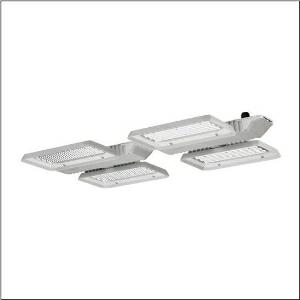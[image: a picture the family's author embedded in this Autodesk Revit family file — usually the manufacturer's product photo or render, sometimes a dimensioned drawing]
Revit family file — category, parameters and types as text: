
# Revit family: highbay_11_51hla1d24nca
name_source: partatom
category: Lighting Fixtures
units: mm (PartAtom-declared; Revit-internal decimal feet)

## family parameters
Cut with Voids When Loaded = No
Host = Face
Light Source = No
Part Type = Normal
Room Calculation Point = No
Round Connector Dimension = Use Diameter
Shared = No

## types (1)
- --- (1 x LED, 32370 lm, 189.6 W, 4000K)
    Apparent Load = 190 VA
    CIE Flux Codes = 88 95 99 100 99
    Color Rendering = 80
    Color Temperature = 4000K
    Default Elevation = 1800 mm
    Description = Highbay 11, LED high bay luminaire, primary light control with lens, of PMMA, light emission: direct distribution, primary light characteristic: symmetric, installation type: suspended mounting, surface-mounted, for 2x 2 x LED rated luminous flux: 32.370 lm, light colour: 840, colour temperature: 4000K, control gear: ECG DALI, with terminal, 5-pole, max. 2.5mm², mains connection: 230..240V, AC, 50/60Hz, rated input power: 190W, LED unit, of diecast aluminium, unplated, bead blasted, silver, length: 940 mm, width: 500 mm, height: 65mm, housing, of diecast aluminium, uncoated, bead blasted, silver, protection rating (complete): IP65, insulation class (complete): insulation class I (protective earthing), certification: CE, ENEC, VDE, protection symbol: D, impact resistance: IK08 with glass or PC cover, permissible ambient temperature for indoor applications: -35..+45°C, reducing of maximum allowable ambient temperature of 5°C with ceiling mounting, corresponds to IFS (International Featured Standards) requirements for safety and quality in the food industry, packaging unit: 1 piece
    Height = 95 mm
    Lamp = 1 x LED
    Lamp Light Flux = 32370 lm
    Lamp Power = 189.6 W
    Lamp count = 1
    Length = 939 mm
    Luminous efficacy = 171 lm/W
    Manufacturer = Siteco
    ModVariant = No
    Model = 51HLA1D24NCA
    Mounting Place = Ceiling
    Mounting Type = Pendant
    Number of Poles = 1
    OnlyDefault = Yes
    Power Factor = 1
    Product Name = Highbay 11
    Product group = LED high bay luminaire
    ProductGroupID = 903
    Protection Class = Protection class I
    Protection Degree = IP 65
    RLX_Detail_Level = 1
    RlxData = <blob elided: 99641 chars, md5=ac518002>
    Socket = socket
    Standby Power = 0 W
    System Light Flux = 32370 lm
    System Power = 190 W
    Type Comments = factory setting: luminous flux: 100 % | dim-lin: 254 | 535 mA
    Type Image = l_1003428.jpg
    URL = http://relux.com
    VarID = @adj_141087
    Voltage = 0 V
    Weight = 0.00 kg
    Width = 501 mm

## geometry (parser evidence)
native form markers: Blend x4, Sweep x10
no freeform markers — native parametric forms only
